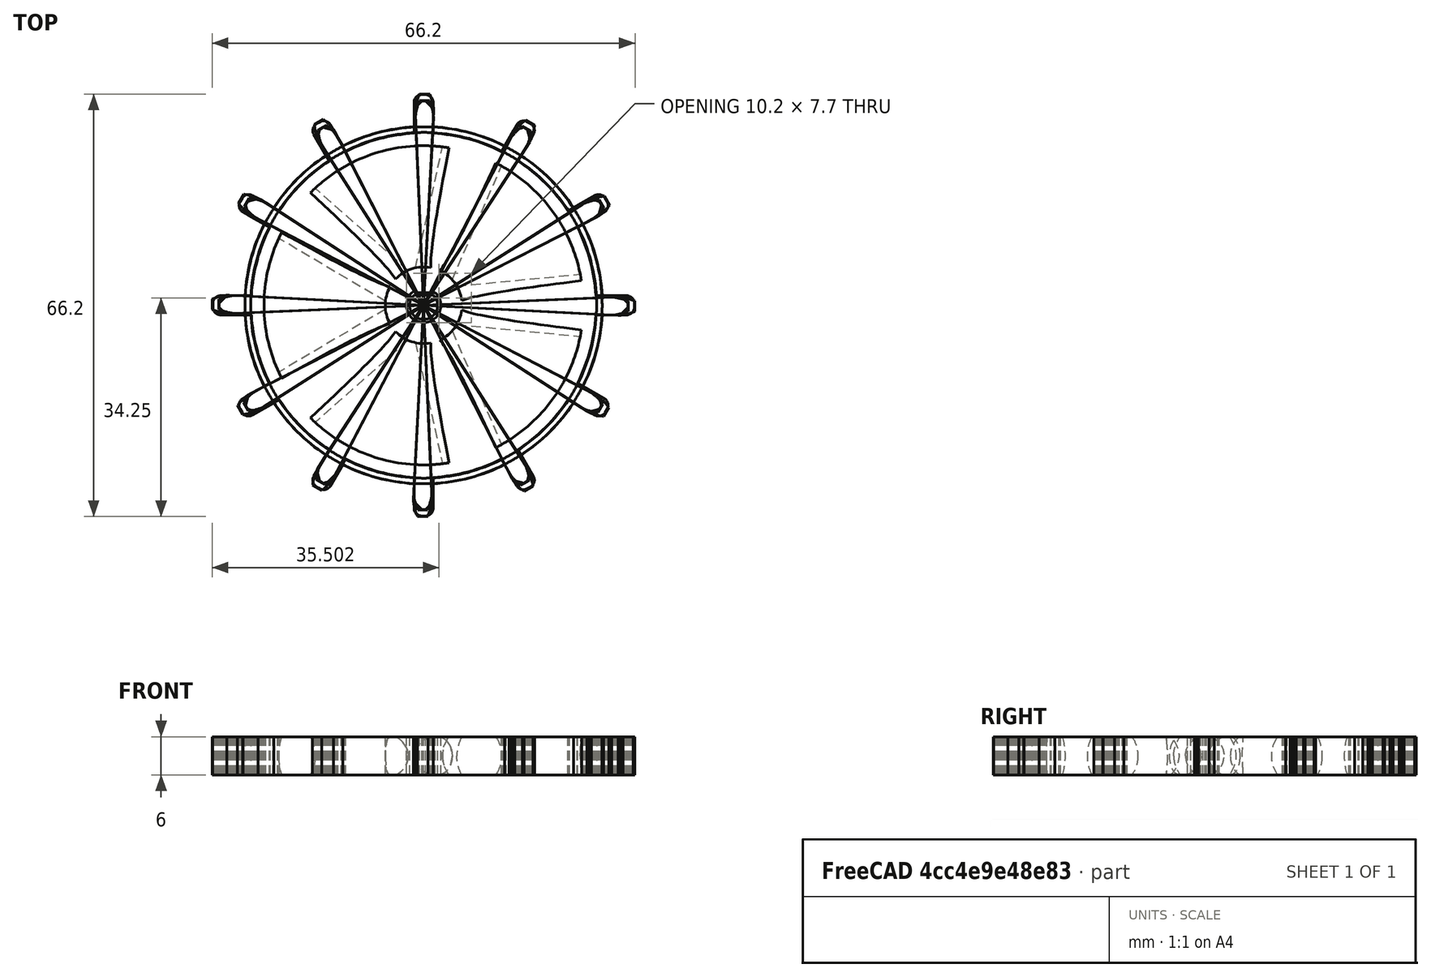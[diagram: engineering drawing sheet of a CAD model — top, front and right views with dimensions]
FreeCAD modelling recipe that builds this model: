
FCSTD DOCUMENT  (FreeCAD 0.17R13541 (Git))
Label: gear_halfcircle_correctsize
License: All rights reserved
LicenseURL: http://en.wikipedia.org/wiki/All_rights_reserved
objects: Part::MultiFuse×23, Part::Cylinder×10, Part::Cut×7, Part::Box×6, Part::Chamfer×6, Part::Fillet×6, Part::Feature×2, Part::Extrusion×2, Part::Cone×1
note: 63 computed .brp shape members not serialized (recipe doc carries the construction recipe); baked Part::Feature solids carry a one-line shape summary decoded from their .brp

FEATURE [Part::Feature] GearFlat
  shape: bbox 64.12 x 64.12 x 2.5e-07 mm, 36 faces, 0 solids (baked)
FEATURE [Part::Extrusion] Gear3D
  Base = -> GearFlat
  Dir = (0,0,6)
  DirMode = 0
  FaceMakerClass = Part::FaceMakerExtrusion
  LengthFwd = 0
  LengthRev = 0
  Placement = pos=(0,0,0) rot=(0,0,-1;0.05236rad)
  Solid = false
  Symmetric = false
FEATURE [Part::Box] Box
  AttacherType = Attacher::AttachEngine3D
  Height = 6
  Length = 3
  Placement = pos=(-1.5,-32,0) rot=(0,0,1;0rad)
  Width = 64
FEATURE [Part::Chamfer] Chamfer
  Base = -> Box
  Edges = 4 edges r=1.2: [Edge1,Edge3,Edge5,Edge7]
FEATURE [Part::Chamfer] Chamfer001
  Base = -> Box
  Edges = 4 edges r=1.2: [Edge1,Edge3,Edge5,Edge7]
  Placement = pos=(0,0,0) rot=(0,0,1;0.523599rad)
FEATURE [Part::Chamfer] Chamfer002
  Base = -> Box
  Edges = 4 edges r=1.2: [Edge1,Edge3,Edge5,Edge7]
  Placement = pos=(0,0,0) rot=(0,0,1;1.0472rad)
FEATURE [Part::Chamfer] Chamfer003
  Base = -> Box
  Edges = 4 edges r=1.2: [Edge1,Edge3,Edge5,Edge7]
  Placement = pos=(0,0,0) rot=(0,0,1;1.5708rad)
FEATURE [Part::Chamfer] Chamfer004
  Base = -> Box
  Edges = 4 edges r=1.2: [Edge1,Edge3,Edge5,Edge7]
  Placement = pos=(0,0,0) rot=(0,0,1;2.0944rad)
FEATURE [Part::Chamfer] Chamfer005
  Base = -> Box
  Edges = 4 edges r=1.2: [Edge1,Edge3,Edge5,Edge7]
  Placement = pos=(0,0,0) rot=(0,0,1;2.61799rad)
FEATURE [Part::MultiFuse] Fusion
  Shapes = -> [Chamfer,Chamfer001]
FEATURE [Part::MultiFuse] Fusion001
  Shapes = -> [Chamfer005,Fusion]
FEATURE [Part::MultiFuse] Fusion002
  Shapes = -> [Chamfer004,Fusion001]
FEATURE [Part::MultiFuse] Fusion003
  Shapes = -> [Chamfer003,Fusion002]
FEATURE [Part::MultiFuse] Fusion004
  Shapes = -> [Chamfer002,Fusion003]
FEATURE [Part::Cylinder] Cylinder
  Angle = 360
  AttacherType = Attacher::AttachEngine3D
  Height = 6
  Radius = 27
FEATURE [Part::Cylinder] Cylinder001
  Angle = 360
  AttacherType = Attacher::AttachEngine3D
  Height = 6
  Radius = 23
FEATURE [Part::Cut] Cut
  Base = -> Fusion004
  Tool = -> Cylinder001
FEATURE [Part::MultiFuse] Fusion005
  Shapes = -> [Cut,Cylinder]
FEATURE [Part::Cylinder] Cylinder002
  Angle = 360
  AttacherType = Attacher::AttachEngine3D
  Height = 6
  Radius = 2.7
FEATURE [Part::Cut] Cut001
  Base = -> Fusion005
  Tool = -> Cylinder002
FEATURE [Part::Box] Box001
  AttacherType = Attacher::AttachEngine3D
  Height = 6
  Length = 9
  Placement = pos=(-1.5,2,0) rot=(0,0,1;0rad)
  Width = 3
FEATURE [Part::MultiFuse] Fusion006
  Shapes = -> [Cut001,Box001]
FEATURE [Part::Feature] GearFlat001
  shape: bbox 66.19 x 66.19 x 2.5e-07 mm, 36 faces, 0 solids (baked)
FEATURE [Part::Extrusion] Gear3D001
  Base = -> GearFlat001
  Dir = (0,0,6)
  DirMode = 0
  FaceMakerClass = Part::FaceMakerExtrusion
  LengthFwd = 0
  LengthRev = 0
  Placement = pos=(0,0,0) rot=(0,0,-1;0.05236rad)
  Solid = false
  Symmetric = false
FEATURE [Part::Box] Box002
  AttacherType = Attacher::AttachEngine3D
  Height = 6
  Length = 3
  Placement = pos=(-1.5,-33,0) rot=(0,0,1;0rad)
  Width = 66
FEATURE [Part::Fillet] Fillet
  Base = -> Box002
  Edges = 4 edges r=1.2: [Edge1,Edge3,Edge5,Edge7]
FEATURE [Part::Fillet] Fillet001
  Base = -> Box002
  Edges = 4 edges r=1.2: [Edge1,Edge3,Edge5,Edge7]
  Placement = pos=(0,0,0) rot=(0,0,1;0.523599rad)
FEATURE [Part::Fillet] Fillet002
  Base = -> Box002
  Edges = 4 edges r=1.2: [Edge1,Edge3,Edge5,Edge7]
  Placement = pos=(0,0,0) rot=(0,0,1;1.0472rad)
FEATURE [Part::Fillet] Fillet003
  Base = -> Box002
  Edges = 4 edges r=1.2: [Edge1,Edge3,Edge5,Edge7]
  Placement = pos=(0,0,0) rot=(0,0,1;1.5708rad)
FEATURE [Part::Fillet] Fillet004
  Base = -> Box002
  Edges = 4 edges r=1.2: [Edge1,Edge3,Edge5,Edge7]
  Placement = pos=(0,0,0) rot=(0,0,1;2.0944rad)
FEATURE [Part::Fillet] Fillet005
  Base = -> Box002
  Edges = 4 edges r=1.2: [Edge1,Edge3,Edge5,Edge7]
  Placement = pos=(0,0,0) rot=(0,0,1;2.61799rad)
FEATURE [Part::Cylinder] Cylinder003
  Angle = 360
  AttacherType = Attacher::AttachEngine3D
  Height = 6
  Radius = 28
FEATURE [Part::MultiFuse] Fusion007
  Shapes = -> [Fillet,Fillet001]
FEATURE [Part::MultiFuse] Fusion008
  Shapes = -> [Fillet002,Fillet003]
FEATURE [Part::MultiFuse] Fusion009
  Shapes = -> [Fillet004,Fillet005]
FEATURE [Part::MultiFuse] Fusion010
  Shapes = -> [Fusion007,Fusion008]
FEATURE [Part::MultiFuse] Fusion011
  Shapes = -> [Fusion009,Fusion010]
FEATURE [Part::Cylinder] Cylinder003001
  Angle = 360
  AttacherType = Attacher::AttachEngine3D
  Height = 6
  Radius = 25
FEATURE [Part::Cut] Cut002
  Base = -> Fusion011
  Tool = -> Cylinder003001
FEATURE [Part::Cylinder] Cylinder003002
  Angle = 360
  AttacherType = Attacher::AttachEngine3D
  Height = 6
  Radius = 25
FEATURE [Part::MultiFuse] Fusion012
  Shapes = -> [Cylinder003,Cut002]
FEATURE [Part::Cut] Cut003
  Base = -> Fusion012
  Tool = -> Cylinder003002
FEATURE [Part::Cylinder] Cylinder003003
  Angle = 360
  AttacherType = Attacher::AttachEngine3D
  Height = 6
  Radius = 6
FEATURE [Part::Cylinder] Cylinder003003001  label="inner_cyl"
  Angle = 360
  AttacherType = Attacher::AttachEngine3D
  Height = 10
  Radius = 2.2
FEATURE [Part::Cut] Cut004
  Base = -> Cylinder003003
  Tool = -> Cylinder003003001
FEATURE [Part::Box] Box003  label="inner_box"
  AttacherType = Attacher::AttachEngine3D
  Height = 6
  Length = 3
  Placement = pos=(-1.5,1.6,0) rot=(0,0,1;0rad)
  Width = 3.6
FEATURE [Part::Cone] Cone
  Angle = 360
  AttacherType = Attacher::AttachEngine3D
  Height = 21
  Placement = pos=(5,0,3) rot=(0,1,0;1.5708rad)
  Radius1 = 3
  Radius2 = 5
FEATURE [Part::Cylinder] Cylinder003003002
  Angle = 360
  AttacherType = Attacher::AttachEngine3D
  Height = 10
  Radius = 2
FEATURE [Part::MultiFuse] Fusion013001
  Shapes = -> [Cylinder003003002,Cone]
FEATURE [Part::MultiFuse] Fusion013002
  Placement = pos=(0,0,0) rot=(0,0,1;1.25664rad)
  Shapes = -> [Cylinder003003002,Cone]
FEATURE [Part::MultiFuse] Fusion013003
  Placement = pos=(0,0,0) rot=(0,0,1;2.51327rad)
  Shapes = -> [Cylinder003003002,Cone]
FEATURE [Part::MultiFuse] Fusion013004
  Placement = pos=(0,0,0) rot=(0,0,1;3.76991rad)
  Shapes = -> [Cylinder003003002,Cone]
FEATURE [Part::MultiFuse] Fusion013005
  Placement = pos=(0,0,0) rot=(0,0,-1;1.25664rad)
  Shapes = -> [Cylinder003003002,Cone]
FEATURE [Part::MultiFuse] Fusion013006
  Shapes = -> [Fusion013001,Fusion013003,Fusion013002,Fusion013004,Fusion013005]
FEATURE [Part::Cylinder] Cylinder003003003
  Angle = 360
  AttacherType = Attacher::AttachEngine3D
  Height = 10
  Radius = 2
FEATURE [Part::Cut] Cut005
  Base = -> Fusion013006
  Tool = -> Cylinder003003003
FEATURE [Part::Box] Box004
  AttacherType = Attacher::AttachEngine3D
  Height = 5
  Length = 100
  Placement = pos=(-50,-50,6) rot=(0,0,1;0rad)
  Width = 100
FEATURE [Part::Box] Box004001
  AttacherType = Attacher::AttachEngine3D
  Height = 5
  Length = 100
  Placement = pos=(-50,-50,-5) rot=(0,0,1;0rad)
  Width = 100
FEATURE [Part::MultiFuse] Fusion013007
  Shapes = -> [Box004,Box004001]
FEATURE [Part::Cut] Cut006
  Base = -> Cut005
  Tool = -> Fusion013007
FEATURE [Part::MultiFuse] Fusion013008
  Shapes = -> [Cut003,Cut004]
FEATURE [Part::MultiFuse] Fusion013009
  Shapes = -> [Box003,Cut006]
FEATURE [Part::MultiFuse] Fusion013010
  Shapes = -> [Fusion013008,Fusion013009]
